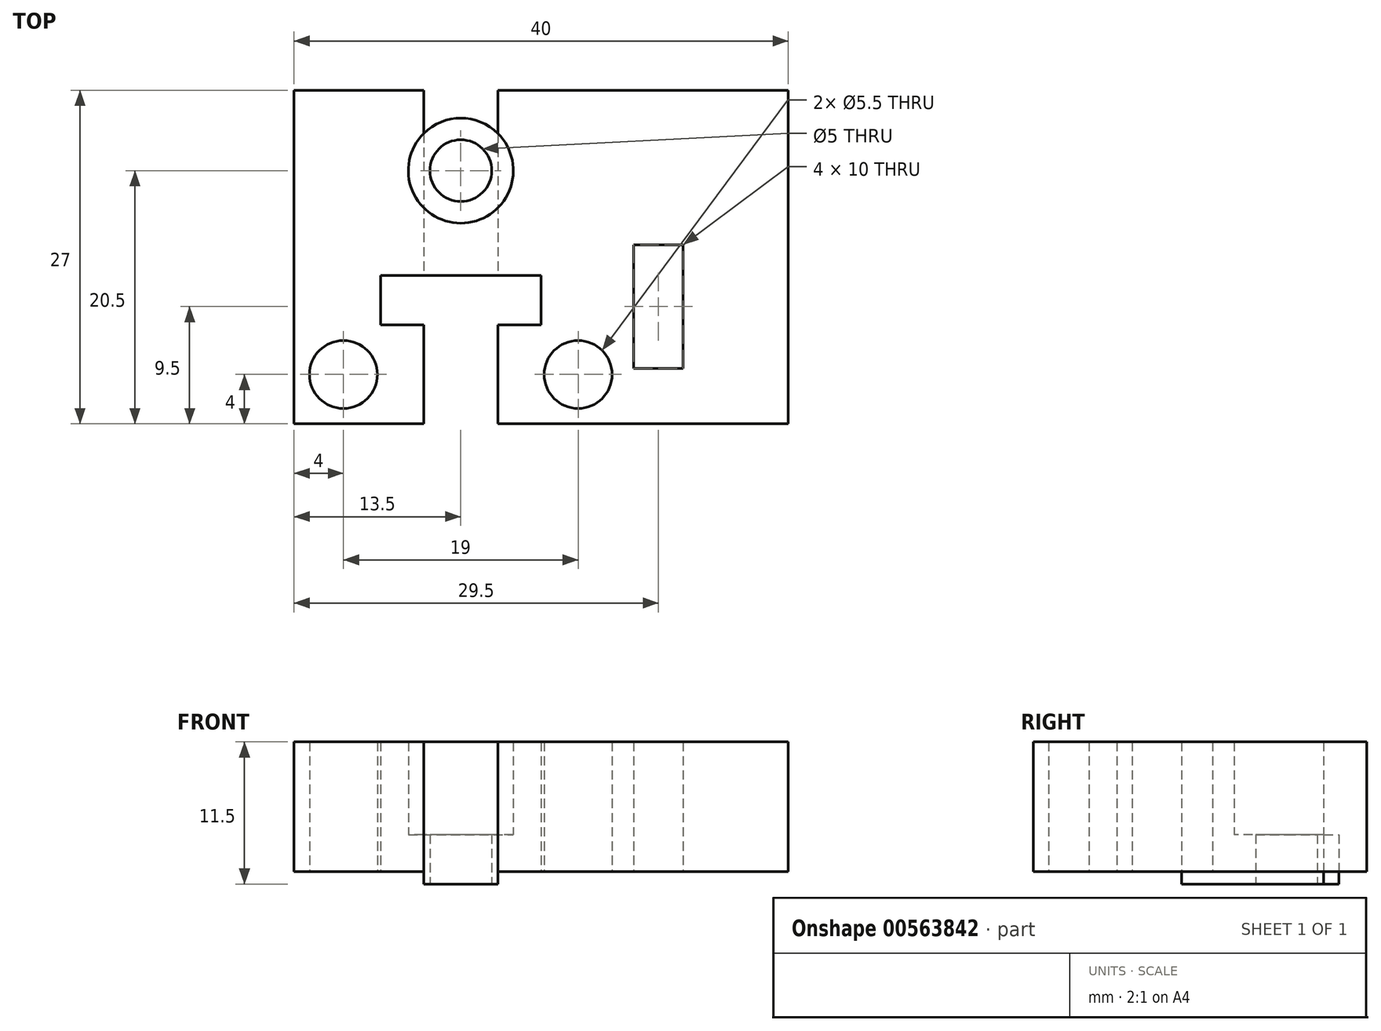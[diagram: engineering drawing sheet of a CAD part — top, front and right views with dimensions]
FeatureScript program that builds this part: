
annotation { "Feature Type Name" : "Feature", "Feature Type Description" : "" }
export const myFeature = defineFeature(function(context is Context, id is Id, definition is map)
    precondition{}
    {
        {
            var Q0;
            Q0=qCreatedBy(makeId("Top.planeOp"),FACE);
            var sketch = newSketch(context, id + "F0", { "sketchPlane" : qUnion([Q0])});
            skLineSegment(sketch, "E0.bottom", {"start": v(20, -13.5) * mm, "end": v(-20, -13.5) * mm});
            skLineSegment(sketch, "E0.top", {"start": v(20, 13.5) * mm, "end": v(-20, 13.5) * mm});
            skLineSegment(sketch, "E0.left", {"start": v(20, -13.5) * mm, "end": v(20, 13.5) * mm});
            skLineSegment(sketch, "E0.right", {"start": v(-20, -13.5) * mm, "end": v(-20, 13.5) * mm});
            skPoint(sketch, "E0.middle", {"position": v(0, 0) * mm});
            skPoint(sketch, "E1", {"position": v(-6.5, 7) * mm});
            skPoint(sketch, "E2", {"position": v(-16, -9.5) * mm});
            skPoint(sketch, "E3", {"position": v(3, -9.5) * mm});
            skCircle(sketch, "E4", {"center": v(-6.5, 7) * mm, "radius": 4.25 * mm});
            skCircle(sketch, "E5", {"center": v(-6.5, 7) * mm, "radius": 2.5 * mm});
            skCircle(sketch, "E6", {"center": v(-16, -9.5) * mm, "radius": 2.75 * mm});
            skCircle(sketch, "E7", {"center": v(3, -9.5) * mm, "radius": 2.75 * mm});
            skLineSegment(sketch, "E8.bottom", {"start": v(-9.5, 13.5) * mm, "end": v(-3.5, 13.5) * mm});
            skLineSegment(sketch, "E8.top", {"start": v(-9.5, -13.5) * mm, "end": v(-3.5, -13.5) * mm});
            skLineSegment(sketch, "E8.left", {"start": v(-9.5, 13.5) * mm, "end": v(-9.5, -13.5) * mm});
            skLineSegment(sketch, "E8.right", {"start": v(-3.5, 13.5) * mm, "end": v(-3.5, -13.5) * mm});
            skLineSegment(sketch, "E9.bottom", {"start": v(7.5, -9) * mm, "end": v(11.5, -9) * mm});
            skLineSegment(sketch, "E9.top", {"start": v(7.5, 1) * mm, "end": v(11.5, 1) * mm});
            skLineSegment(sketch, "E9.left", {"start": v(7.5, -9) * mm, "end": v(7.5, 1) * mm});
            skLineSegment(sketch, "E9.right", {"start": v(11.5, -9) * mm, "end": v(11.5, 1) * mm});
            skLineSegment(sketch, "E10.bottom", {"start": v(-13, -5.5) * mm, "end": v(0, -5.5) * mm});
            skLineSegment(sketch, "E10.top", {"start": v(-13, -1.5) * mm, "end": v(0, -1.5) * mm});
            skLineSegment(sketch, "E10.left", {"start": v(-13, -5.5) * mm, "end": v(-13, -1.5) * mm});
            skLineSegment(sketch, "E10.right", {"start": v(0, -5.5) * mm, "end": v(0, -1.5) * mm});
            skSolve(sketch);
        }
        {
            var Q0;
            {var subQ13=sQuery(id+"F0.wireOp",EDGE,"E0.right");Q0=makeQuery(id+"F0.imprint","IMPRINT",FACE,{"disambiguationData":[TD([[makeQuery(id+"F0.imprint","IMPRINT",EDGE,{"derivedFrom":subQ13}),-1.0]])]});}
            var Q1;
            {var subQ5=sQuery(id+"F0.wireOp",EDGE,"E8.bottom");Q1=makeQuery(id+"F0.imprint","IMPRINT",FACE,{"disambiguationData":[TD([[makeQuery(id+"F0.imprint","IMPRINT",EDGE,{"derivedFrom":subQ5}),-1.0]])]});}
            var Q2;
            {var subQ0=sQuery(id+"F0.wireOp",EDGE,"E0.left");Q2=makeQuery(id+"F0.imprint","IMPRINT",FACE,{"disambiguationData":[TD([[makeQuery(id+"F0.imprint","IMPRINT",EDGE,{"derivedFrom":subQ0}),1.0]])]});}
            var Q3;
            {var subQ0=sQuery(id+"F0.wireOp",EDGE,"E8.top");Q3=makeQuery(id+"F0.imprint","IMPRINT",FACE,{"disambiguationData":[TD([[makeQuery(id+"F0.imprint","IMPRINT",EDGE,{"derivedFrom":subQ0}),1.0]])]});}
            var Q4;
            {var subQ0=sQuery(id+"F0.wireOp",EDGE,"E8.left");var subQ1=sQuery(id+"F0.wireOp",EDGE,"E4");var subQ2=makeQuery(id+"F0.imprint","INTERSECT",VERTEX,{"disambiguationData":[OD(1.0)],"derivedFrom":[subQ1,subQ0]});Q4=makeQuery(id+"F0.imprint","IMPRINT",FACE,{"disambiguationData":[TD([[makeQuery(id+"F0.imprint","IMPRINT",EDGE,{"disambiguationData":[TD([[subQ2,-1.0]])],"derivedFrom":subQ1}),-1.0]])]});}
            extrude(context, id + "F1", {"entities" : qUnion([Q0, Q1, Q2, Q3, Q4]), "depth" : 10.5 * mm, "offsetDistance" : 25 * mm});
        }
        {
            var Q0;
            {var subQ0=sQuery(id+"F0.wireOp",EDGE,"E8.left");var subQ1=sQuery(id+"F0.wireOp",EDGE,"E4");var subQ2=makeQuery(id+"F0.imprint","INTERSECT",VERTEX,{"disambiguationData":[OD(0.0)],"derivedFrom":[subQ1,subQ0]});Q0=makeQuery(id+"F0.imprint","IMPRINT",FACE,{"disambiguationData":[TD([[makeQuery(id+"F0.imprint","IMPRINT",EDGE,{"disambiguationData":[TD([[subQ2,-1.0]])],"derivedFrom":subQ1}),1.0]])]});}
            var Q1;
            Q1=makeQuery(id+"F0.imprint","IMPRINT",FACE,{"disambiguationData":[TD([[makeQuery(id+"F0.imprint","IMPRINT",EDGE,{"derivedFrom":sQuery(id+"F0.wireOp",EDGE,"E5")}),-1.0]])]});
            var Q2;
            {var subQ0=sQuery(id+"F0.wireOp",EDGE,"E8.right");var subQ1=sQuery(id+"F0.wireOp",EDGE,"E4");var subQ2=makeQuery(id+"F0.imprint","INTERSECT",VERTEX,{"disambiguationData":[OD(0.0)],"derivedFrom":[subQ1,subQ0]});Q2=makeQuery(id+"F0.imprint","IMPRINT",FACE,{"disambiguationData":[TD([[makeQuery(id+"F0.imprint","IMPRINT",EDGE,{"disambiguationData":[TD([[subQ2,1.0]])],"derivedFrom":subQ1}),1.0]])]});}
            extrude(context, id + "F2", {"entities" : qUnion([Q0, Q1, Q2]), "operationType" : NewBodyOperationType.ADD, "depth" : 3 * mm, "offsetDistance" : 25 * mm});
        }
        {
            var Q0;
            {var subQ5=sQuery(id+"F0.wireOp",EDGE,"E8.bottom");Q0=makeQuery(id+"F0.imprint","IMPRINT",FACE,{"disambiguationData":[TD([[makeQuery(id+"F0.imprint","IMPRINT",EDGE,{"derivedFrom":subQ5}),-1.0]])]});}
            var Q1;
            Q1=makeQuery(id+"F0.imprint","IMPRINT",FACE,{"disambiguationData":[TD([[makeQuery(id+"F0.imprint","IMPRINT",EDGE,{"derivedFrom":sQuery(id+"F0.wireOp",EDGE,"E5")}),-1.0]])]});
            var Q2;
            {var subQ0=sQuery(id+"F0.wireOp",EDGE,"E8.left");var subQ1=sQuery(id+"F0.wireOp",EDGE,"E4");var subQ2=makeQuery(id+"F0.imprint","INTERSECT",VERTEX,{"disambiguationData":[OD(1.0)],"derivedFrom":[subQ1,subQ0]});Q2=makeQuery(id+"F0.imprint","IMPRINT",FACE,{"disambiguationData":[TD([[makeQuery(id+"F0.imprint","IMPRINT",EDGE,{"disambiguationData":[TD([[subQ2,-1.0]])],"derivedFrom":subQ1}),-1.0]])]});}
            var Q3;
            {var subQ0=sQuery(id+"F0.wireOp",EDGE,"E8.top");Q3=makeQuery(id+"F0.imprint","IMPRINT",FACE,{"disambiguationData":[TD([[makeQuery(id+"F0.imprint","IMPRINT",EDGE,{"derivedFrom":subQ0}),1.0]])]});}
            extrude(context, id + "F3", {"entities" : qUnion([Q0, Q1, Q2, Q3]), "operationType" : NewBodyOperationType.ADD, "oppositeDirection" : true, "depth" : 1 * mm, "offsetDistance" : 25 * mm});
        }
    });
